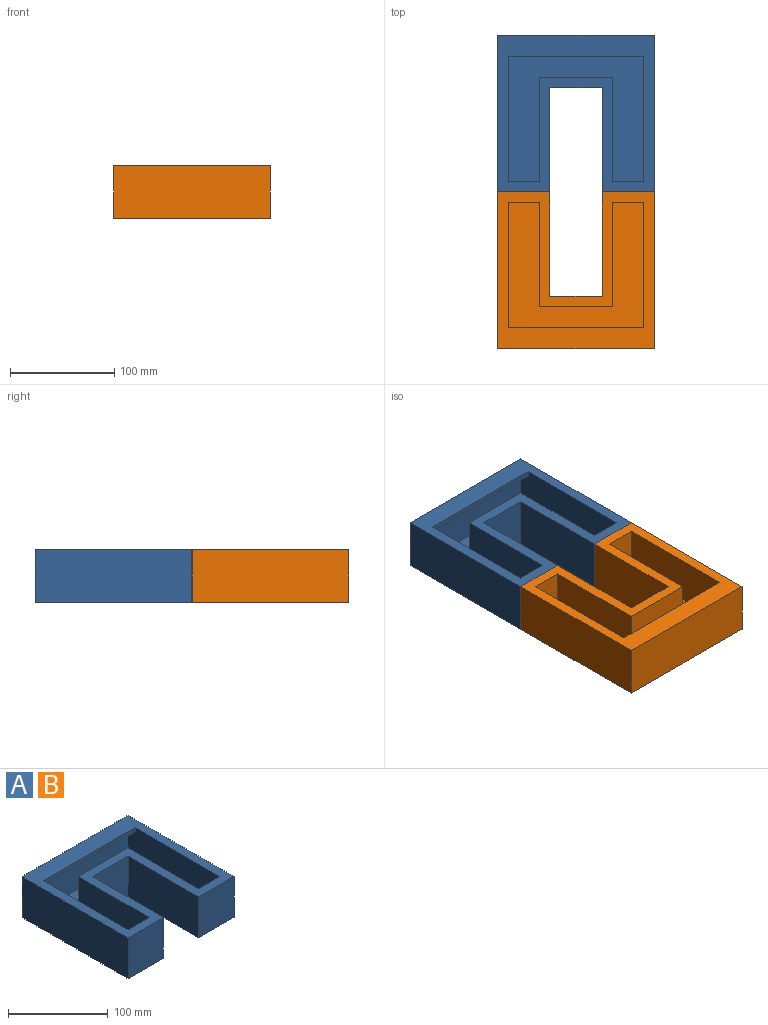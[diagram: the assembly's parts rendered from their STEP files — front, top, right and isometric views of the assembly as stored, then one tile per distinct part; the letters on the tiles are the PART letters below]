
ASSEMBLY  parts=2 mates=1
PART A: 21 faces, bbox 150x150x50 mm
  f0: plane 130x40mm, normal (0,-1,0), area 5200mm2, adj f1,f10,f18,f19
  f1: plane 130x45mm, normal (-1,0,0), area 5800mm2, adj f0,f11,f17,f18,f19,f20
  f2: plane 150x150mm, normal (0,0,-1), area 17500mm2, adj f3,f4,f5,f6,f7,f8,f9,f16
  f3: plane 150x50mm, normal (-1,0,0), area 7500mm2, adj f2,f4,f16,f17
  f4: plane 50x50mm, normal (0,-1,0), area 2500mm2, adj f2,f3,f5,f17
  f5: plane 100x50mm, normal (1,0,0), area 5000mm2, adj f2,f4,f6,f17
  f6: plane 50x50mm, normal (0,-1,0), area 2500mm2, adj f2,f5,f7,f17
  f7: plane 100x50mm, normal (-1,0,0), area 5000mm2, adj f2,f6,f8,f17
  f8: plane 50x50mm, normal (0,-1,0), area 2500mm2, adj f2,f7,f9,f17
  f9: plane 150x50mm, normal (1,0,0), area 7500mm2, adj f2,f8,f16,f17
  f10: plane 130x45mm, normal (1,0,0), area 5800mm2, adj f0,f15,f17,f18,f19,f20
  f11: plane 45x30mm, normal (0,1,0), area 1350mm2, adj f1,f12,f17,f18
  f12: plane 100x45mm, normal (1,0,0), area 4500mm2, adj f11,f13,f17,f18
  f13: plane 70x45mm, normal (0,1,0), area 3150mm2, adj f12,f14,f17,f18
  f14: plane 100x45mm, normal (-1,0,0), area 4500mm2, adj f13,f15,f17,f18
  f15: plane 45x30mm, normal (0,1,0), area 1350mm2, adj f10,f14,f17,f18
  f16: plane 150x50mm, normal (0,1,0), area 7500mm2, adj f2,f3,f9,f17
  f17: plane 150x150mm, normal (0,0,1), area 8900mm2, adj f1,f3,f4,f5,f6,f7,f8,f9
  f18: plane 130x130mm, normal (0,0,1), area 9900mm2, adj f0,f1,f10,f11,f12,f13,f14,f15
  f19: plane 130x10mm, normal (0,0,-1), area 1300mm2, adj f0,f1,f10,f20
  f20: plane 130x5mm, normal (0,-1,0), area 650mm2, adj f1,f10,f17,f19
PART B: same geometry as A
PLACE A t=(-0.8,-65.56,54.81)mm
PLACE B rot(axis=(0,0,-1),180deg) t=(-150.8,-65.56,54.81)mm
MATE fastened B.f8 <-> A.f4  axis (0,1,0) through (-125.8,-65.56,79.81)mm
